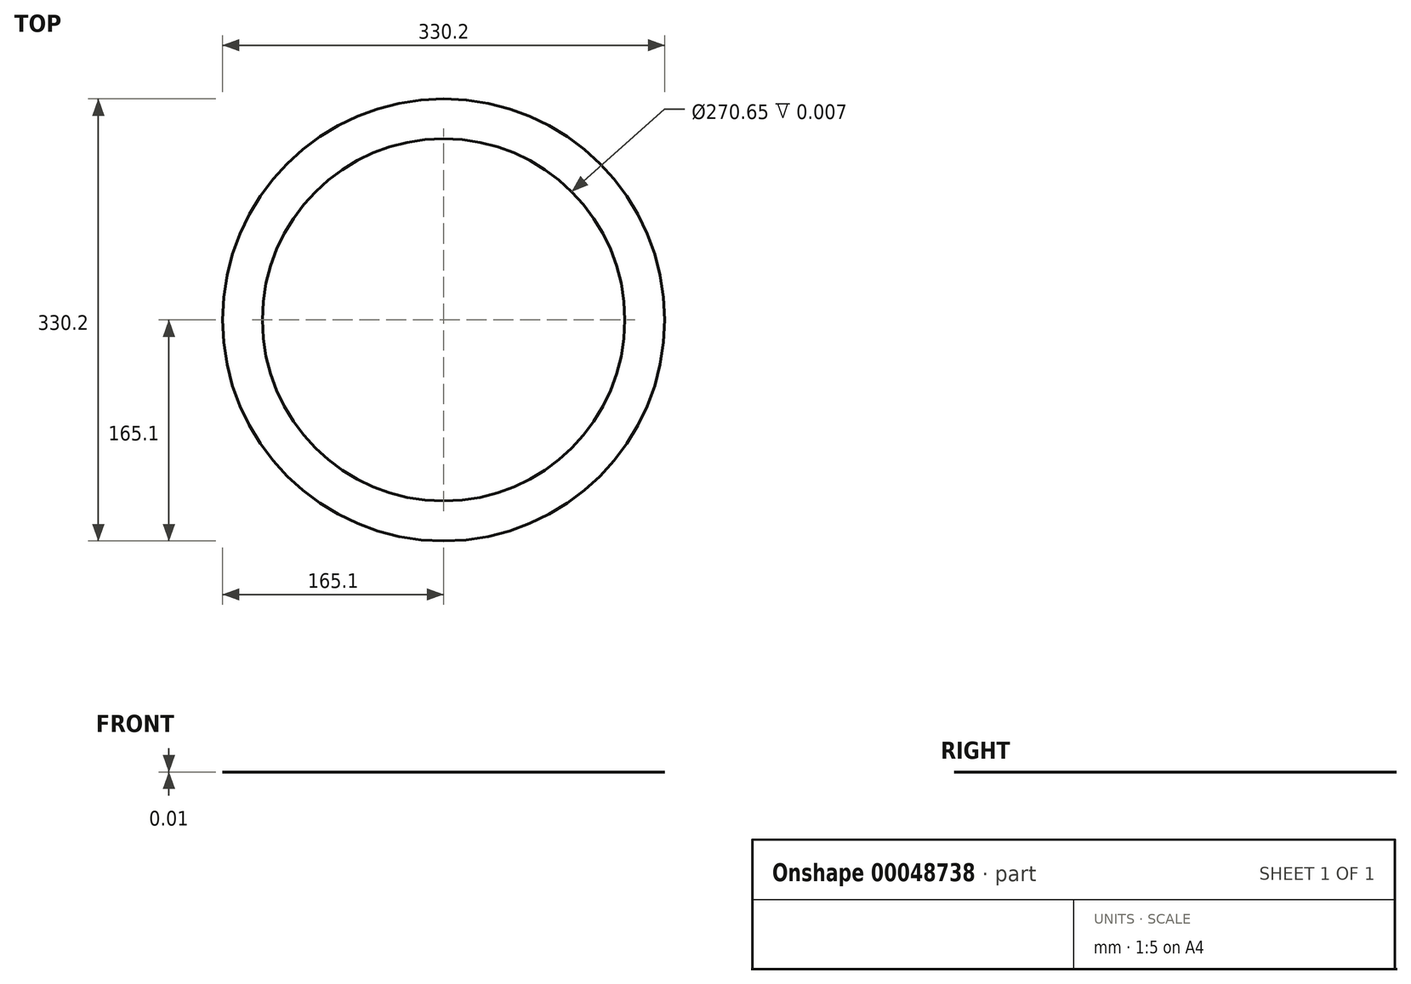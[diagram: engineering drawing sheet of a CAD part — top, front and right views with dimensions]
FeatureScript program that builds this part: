
annotation { "Feature Type Name" : "Feature", "Feature Type Description" : "" }
export const myFeature = defineFeature(function(context is Context, id is Id, definition is map)
    precondition{}
    {
        {
            var Q0;
            Q0=qCreatedBy(makeId("Top.planeOp"),FACE);
            var sketch = newSketch(context, id + "F0", { "sketchPlane" : qUnion([Q0])});
            skCircle(sketch, "E0", {"center": v(0, 0) * mm, "radius": 165.1 * mm});
            skCircle(sketch, "E1", {"center": v(0, 0) * mm, "radius": 135.33 * mm});
            skSolve(sketch);
        }
        {
            var Q0;
            Q0=makeQuery(id+"F0.imprint","IMPRINT",FACE,{"disambiguationData":[TD([[makeQuery(id+"F0.imprint","IMPRINT",EDGE,{"derivedFrom":sQuery(id+"F0.wireOp",EDGE,"E0")}),1.0]])]});
            extrude(context, id + "F1", {"entities" : qUnion([Q0]), "depth" : 3 / 406.4 * mm});
        }
    });
